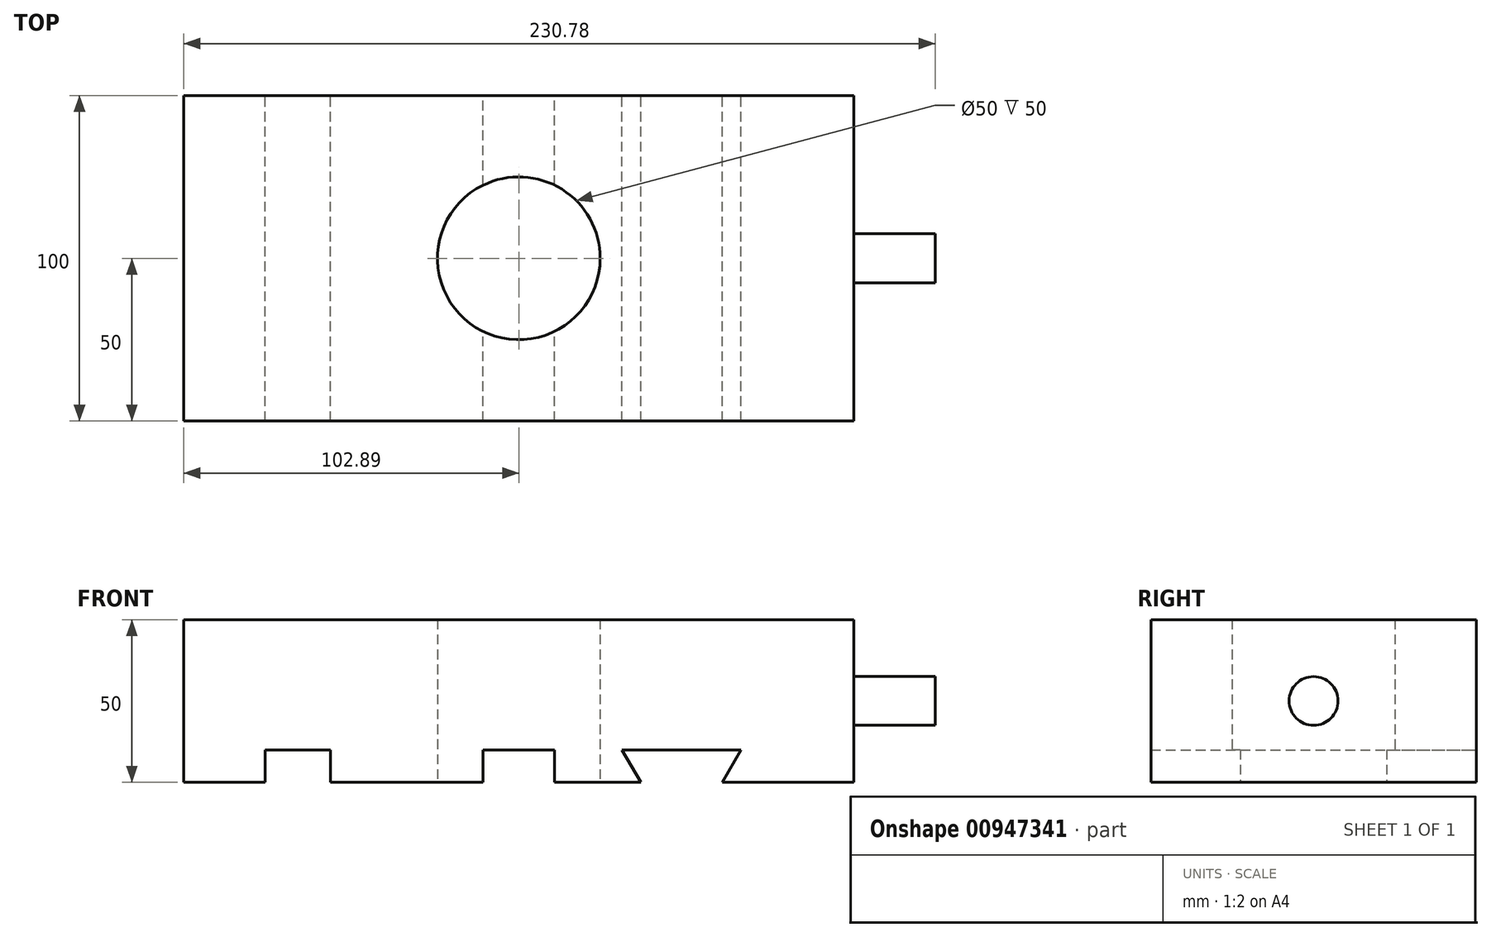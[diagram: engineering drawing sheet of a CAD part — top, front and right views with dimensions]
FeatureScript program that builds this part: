
annotation { "Feature Type Name" : "Feature", "Feature Type Description" : "" }
export const myFeature = defineFeature(function(context is Context, id is Id, definition is map)
    precondition{}
    {
        {
            var Q0;
            Q0=qCreatedBy(makeId("Top.planeOp"),FACE);
            var sketch = newSketch(context, id + "F0", { "sketchPlane" : qUnion([Q0])});
            skLineSegment(sketch, "E0.bottom", {"start": v(102.89, -50) * mm, "end": v(-102.89, -50) * mm});
            skLineSegment(sketch, "E0.top", {"start": v(102.89, 50) * mm, "end": v(-102.89, 50) * mm});
            skLineSegment(sketch, "E0.left", {"start": v(102.89, -50) * mm, "end": v(102.89, 50) * mm});
            skLineSegment(sketch, "E0.right", {"start": v(-102.89, -50) * mm, "end": v(-102.89, 50) * mm});
            skPoint(sketch, "E0.middle", {"position": v(0, 0) * mm});
            skCircle(sketch, "E1", {"center": v(0, 0) * mm, "radius": 25 * mm});
            skSolve(sketch);
        }
        {
            var Q0;
            Q0=makeQuery(id+"F0.imprint","IMPRINT",FACE,{"disambiguationData":[TD([[makeQuery(id+"F0.imprint","IMPRINT",EDGE,{"derivedFrom":sQuery(id+"F0.wireOp",EDGE,"E0.bottom")}),-1.0]])]});
            extrude(context, id + "F1", {"entities" : qUnion([Q0]), "depth" : 50 * mm, "offsetDistance" : 25 * mm});
        }
        {
            var Q0;
            Q0=makeQuery(id+"F1.opExtrude","CAP_FACE",FACE,{"disambiguationData":[OSD([sQuery(id+"F0.wireOp",EDGE,"E0.bottom"),sQuery(id+"F0.wireOp",EDGE,"E0.top"),sQuery(id+"F0.wireOp",EDGE,"E0.left"),sQuery(id+"F0.wireOp",EDGE,"E0.right"),sQuery(id+"F0.wireOp",EDGE,"E1")])],"isStart":true});
            var sketch = newSketch(context, id + "F2", { "sketchPlane" : qUnion([Q0])});
            skLineSegment(sketch, "E2.bottom", {"start": v(-77.89, 50) * mm, "end": v(-57.89, 50) * mm});
            skLineSegment(sketch, "E2.top", {"start": v(-77.89, -50) * mm, "end": v(-57.89, -50) * mm});
            skLineSegment(sketch, "E2.left", {"start": v(-77.89, 50) * mm, "end": v(-77.89, -50) * mm});
            skLineSegment(sketch, "E2.right", {"start": v(-57.89, 50) * mm, "end": v(-57.89, -50) * mm});
            skLineSegment(sketch, "E3", {"start": v(-11, 50) * mm, "end": v(-11, -50) * mm});
            skLineSegment(sketch, "E4", {"start": v(-11, 50) * mm, "end": v(11, 50) * mm});
            skLineSegment(sketch, "E5", {"start": v(11, 50) * mm, "end": v(11, -50) * mm});
            skLineSegment(sketch, "E6", {"start": v(11, -50) * mm, "end": v(-11, -50) * mm});
            skLineSegment(sketch, "E7", {"start": v(0, -50) * mm, "end": v(0, 50) * mm, "construction": true});
            skSolve(sketch);
        }
        {
            var Q0;
            Q0=makeQuery(id+"F2.imprint","IMPRINT",FACE,{"disambiguationData":[TD([[makeQuery(id+"F2.imprint","IMPRINT",EDGE,{"derivedFrom":sQuery(id+"F2.wireOp",EDGE,"E2.bottom")}),1.0]])]});
            var Q1;
            {var subQ0=sQuery(id+"F2.wireOp",EDGE,"E4");Q1=makeQuery(id+"F2.imprint","IMPRINT",FACE,{"disambiguationData":[TD([[makeQuery(id+"F2.imprint","IMPRINT",EDGE,{"derivedFrom":subQ0}),1.0]])]});}
            var Q2;
            {var subQ0=sQuery(id+"F2.wireOp",EDGE,"E6");Q2=makeQuery(id+"F2.imprint","IMPRINT",FACE,{"disambiguationData":[TD([[makeQuery(id+"F2.imprint","IMPRINT",EDGE,{"derivedFrom":subQ0}),-1.0]])]});}
            extrude(context, id + "F3", {"entities" : qUnion([Q0, Q1, Q2]), "operationType" : NewBodyOperationType.REMOVE, "oppositeDirection" : true, "depth" : 10 * mm, "offsetDistance" : 25 * mm});
        }
        {
            var Q0;
            Q0=makeQuery(id+"F1.opExtrude","SWEPT_FACE",FACE,{"disambiguationData":[OSD([sQuery(id+"F0.wireOp",EDGE,"E0.top")])]});
            var sketch = newSketch(context, id + "F4", { "sketchPlane" : qUnion([Q0])});
            skLineSegment(sketch, "E8", {"start": v(-37.5, 0) * mm, "end": v(-31.73, 10) * mm});
            skLineSegment(sketch, "E9", {"start": v(-31.73, 10) * mm, "end": v(-68.27, 10) * mm});
            skLineSegment(sketch, "E10", {"start": v(-68.27, 10) * mm, "end": v(-62.5, 0) * mm});
            skLineSegment(sketch, "E11", {"start": v(-62.5, 0) * mm, "end": v(-37.5, 0) * mm});
            skLineSegment(sketch, "E12", {"start": v(-50, 10) * mm, "end": v(-50, 0) * mm, "construction": true});
            skSolve(sketch);
        }
        {
            var Q0;
            Q0 = qSketchRegion(id + "F4", true);
            extrude(context, id + "F5", {"entities" : qUnion([Q0]), "operationType" : NewBodyOperationType.REMOVE, "endBound" : BoundingType.THROUGH_ALL, "oppositeDirection" : true, "depth" : 25 * mm, "offsetDistance" : 25 * mm});
        }
        {
            var Q0;
            Q0=makeQuery(id+"F1.opExtrude","SWEPT_FACE",FACE,{"disambiguationData":[OSD([sQuery(id+"F0.wireOp",EDGE,"E0.left")])]});
            var sketch = newSketch(context, id + "F6", { "sketchPlane" : qUnion([Q0])});
            skCircle(sketch, "E13", {"center": v(0, 25) * mm, "radius": 7.5 * mm});
            skPoint(sketch, "E13.centerSnap0", {"position": v(-50, 25) * mm});
            skPoint(sketch, "E13.centerSnap1", {"position": v(0, 50) * mm});
            skSolve(sketch);
        }
        {
            var Q0;
            Q0=makeQuery(id+"F6.imprint","IMPRINT",FACE,{"disambiguationData":[TD([[makeQuery(id+"F6.imprint","IMPRINT",EDGE,{"derivedFrom":sQuery(id+"F6.wireOp",EDGE,"E13")}),1.0]])]});
            extrude(context, id + "F7", {"entities" : qUnion([Q0]), "operationType" : NewBodyOperationType.ADD, "depth" : 25 * mm, "offsetDistance" : 25 * mm});
        }
    });
